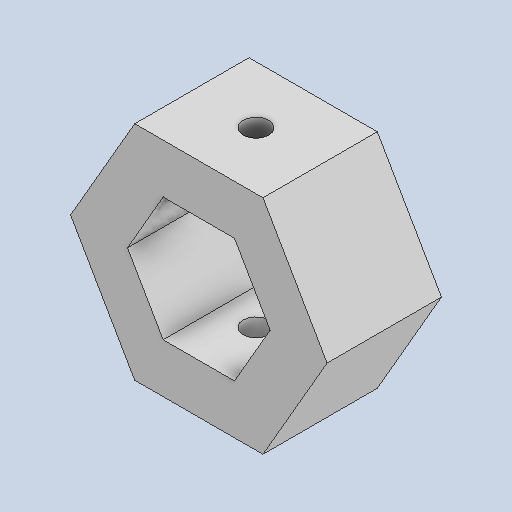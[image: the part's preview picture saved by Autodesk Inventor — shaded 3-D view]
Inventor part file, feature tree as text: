
AUTODESK INVENTOR PART (.ipt)
format: ipt  version: 2022 (Build 260153000, 153)  size: 127,488 bytes
history: native  units: mm
features: extrude x2, sketch x2
ambient origin geometry x8: Origin, YZ Plane, XZ Plane, XY Plane, X Axis, Y Axis, Z Axis, Center Point
bodies: Body1 (feature_tree)
feature tree (4):
  extrude  "Extrusion4"  Depth=60.0mm TaperAngle=360.0deg
  extrude  "Extrusion5"  Depth=2.5mm
  sketch  "Sketch5"  dims[d9=3.1mm d10=60.0mm d12=360.0deg]
  sketch  "Sketch6"  dims[d14=0.45mm d15=2.5mm d16=5.8mm d17=0.0mm d18=1.3mm d19=15.0mm d20=0.0mm]
